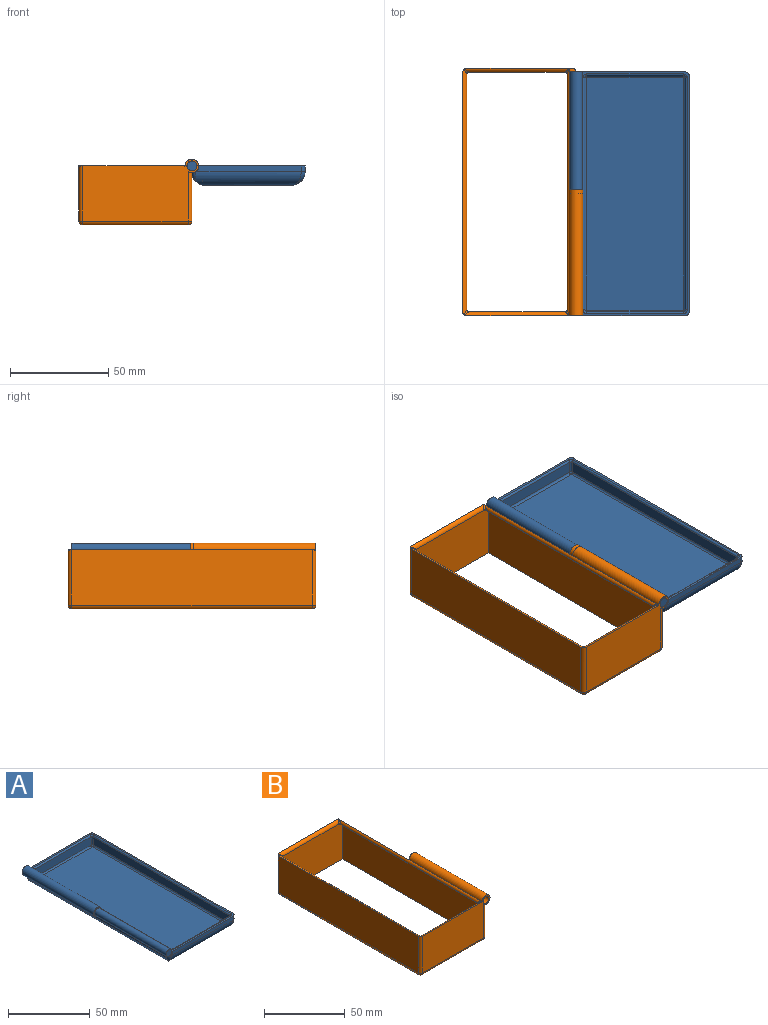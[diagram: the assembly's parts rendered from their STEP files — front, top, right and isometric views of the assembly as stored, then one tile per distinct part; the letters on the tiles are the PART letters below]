
ASSEMBLY  parts=2 mates=1
PART A: 48 faces, bbox 60.8x125.2x13.2 mm
  f0: cylinder r=7mm len=53.5mm, axis (1,0,0), area 556.8mm2, adj f5,f7,f40,f42,f45
  f1: plane 124x54.2mm, normal (0,0,1), area 244.1mm2, adj f2,f4,f5,f6,f8,f9,f19,f23
  f2: cylinder r=3.3mm len=62mm, axis (0,1,0), area 965mm2, adj f1,f3,f4,f5,f39,f45,f46
  f3: plane 119.94x1.63mm, normal (-1,0,0), area 182.9mm2, adj f2,f4,f6,f40,f45,f47
  f4: plane 6.8x6.8mm, normal (0,-1,0), area 15.6mm2, adj f1,f2,f3,f6,f10
  f5: plane 58.8x6.16mm, normal (0,1,0), area 183.8mm2, adj f0,f1,f2,f39,f41,f46
  f6: cylinder r=3.5mm len=62mm, axis (0,1,0), area 340mm2, adj f1,f3,f4,f9,f33,f38,f47
  f7: plane 110x43.81mm, normal (0,0,-1), area 4819.5mm2, adj f0,f37,f38,f40
  f8: plane 120x2.86mm, normal (1,0,0), area 343mm2, adj f1,f37,f41,f43
  f9: plane 53.48x2.86mm, normal (0,-1,0), area 149.9mm2, adj f1,f6,f38,f43
  f10: cylinder r=2.5mm len=62mm, axis (0,1,0), area 973.9mm2, adj f4,f11
  f11: plane 5x5mm, normal (0,-1,0), area 19.6mm2, adj f10
  f12: plane 118x6mm, normal (1,0,0), area 708mm2, adj f25,f30,f33,f36
  f13: plane 49x6mm, normal (0,1,0), area 294mm2, adj f22,f31,f32,f36
  f14: plane 118x6mm, normal (-1,0,0), area 708mm2, adj f17,f21,f22,f23
  f15: plane 49x6mm, normal (0,-1,0), area 294mm2, adj f17,f20,f24,f25
  f16: plane 118x49mm, normal (0,0,1), area 5782mm2, adj f20,f21,f30,f31
  f17: cylinder r=1mm len=6mm, axis (0,0,-1), area 9.4mm2, adj f14,f15,f18,f19
  f18: sphere r=1mm, area 1.6mm2, adj f17,f20,f21
  f19: torus R=2mm, axis (0,0,-1), area 3.4mm2, adj f1,f17,f23,f24
  f20: cylinder r=1mm len=49mm, axis (-1,0,0), area 77mm2, adj f15,f16,f18,f26
  f21: cylinder r=1mm len=118mm, axis (0,1,0), area 185.4mm2, adj f14,f16,f18,f27
  f22: cylinder r=1mm len=6mm, axis (0,0,1), area 9.4mm2, adj f13,f14,f27,f28
  f23: cylinder r=1mm len=118mm, axis (0,1,0), area 185.4mm2, adj f1,f14,f19,f28
  f24: cylinder r=1mm len=49mm, axis (-1,0,0), area 77mm2, adj f1,f15,f19,f29
  f25: cylinder r=1mm len=6mm, axis (0,0,1), area 9.4mm2, adj f12,f15,f26,f29
  f26: sphere r=1mm, area 1.6mm2, adj f20,f25,f30
  f27: sphere r=1mm, area 1.6mm2, adj f21,f22,f31
  f28: torus R=2mm, axis (0,0,-1), area 3.4mm2, adj f1,f22,f23,f32
  f29: torus R=2mm, axis (0,0,-1), area 3.4mm2, adj f1,f24,f25,f33
  f30: cylinder r=1mm len=118mm, axis (0,-1,0), area 185.4mm2, adj f12,f16,f26,f34
  f31: cylinder r=1mm len=49mm, axis (1,0,0), area 77mm2, adj f13,f16,f27,f34
  f32: cylinder r=1mm len=49mm, axis (1,0,0), area 77mm2, adj f1,f13,f28,f35
  f33: cylinder r=1mm len=118mm, axis (0,-1,0), area 185.4mm2, adj f1,f6,f12,f29,f35
  f34: sphere r=1mm, area 1.6mm2, adj f30,f31,f36
  f35: torus R=2mm, axis (0,0,-1), area 3.4mm2, adj f1,f32,f33,f36
  f36: cylinder r=1mm len=6mm, axis (0,0,-1), area 9.4mm2, adj f12,f13,f34,f35
  f37: cylinder r=7mm len=120mm, axis (0,-1,0), area 1279.5mm2, adj f7,f8,f42,f44
  f38: cylinder r=7mm len=53.5mm, axis (-1,0,0), area 556.8mm2, adj f6,f7,f9,f40,f44,f47
  f39: cylinder r=7mm len=3.3mm, axis (1,0,0), area 1mm2, adj f2,f5
  f40: cylinder r=7mm len=120.84mm, axis (0,1,0), area 1042.7mm2, adj f0,f3,f7,f38,f45,f47
  f41: cylinder r=2mm len=2.86mm, axis (0,0,1), area 9mm2, adj f1,f5,f8,f42
  f42: bspline ~8.17x7mm, area 23.6mm2, adj f0,f37,f41
  f43: cylinder r=2mm len=2.86mm, axis (0,0,-1), area 9mm2, adj f1,f8,f9,f44
  f44: bspline ~8.17x7mm, area 23.6mm2, adj f37,f38,f43
  f45: torus R=5mm, axis (-1,0,0), area 10.7mm2, adj f0,f2,f3,f40,f46
  f46: cylinder r=2mm len=0.35mm, axis (0,0,1), area 0mm2, adj f2,f5,f45
  f47: torus R=5mm, axis (-1,0,0), area 10.1mm2, adj f3,f6,f38,f40
PART B: 38 faces, bbox 61x126.5x33.5 mm
  f0: plane 120.02x0.27mm, normal (-1,0,0), area 32.2mm2, adj f13,f19,f20,f36
  f1: plane 122x24.5mm, normal (1,0,0), area 2989mm2, adj f2,f14,f22,f23,f24
  f2: cylinder r=3.5mm len=64mm, axis (0,1,0), area 1056.4mm2, adj f1,f5,f13,f15,f21,f22
  f3: plane 122x28mm, normal (-1,0,0), area 3416mm2, adj f10,f27,f30,f33
  f4: cylinder r=2.55mm len=64mm, axis (0,1,0), area 1025.4mm2, adj f5,f15
  f5: plane 59x31.5mm, normal (0,-1,0), area 1513mm2, adj f2,f4,f12,f21,f22,f27,f28
  f6: plane 53.5x28.03mm, normal (0,1,0), area 1495mm2, adj f11,f14,f17,f24,f29,f30
  f7: plane 122x28mm, normal (1,0,0), area 3416mm2, adj f8,f9,f10,f33,f34,f35
  f8: plane 53.5x28mm, normal (0,1,0), area 1498mm2, adj f7,f12,f28,f35,f36,f37
  f9: plane 53.5x28mm, normal (0,-1,0), area 1497.6mm2, adj f7,f11,f14,f29,f34,f36,f37
  f10: cylinder r=2mm len=124.58mm, axis (0,1,0), area 384.7mm2, adj f3,f7,f16,f18,f27,f30
  f11: cylinder r=2mm len=53.05mm, axis (1,0,0), area 159.4mm2, adj f6,f9,f16,f17,f19,f30
  f12: cylinder r=2mm len=53.05mm, axis (-1,0,0), area 159.4mm2, adj f5,f8,f18,f20,f21,f27
  f13: cylinder r=2mm len=124.23mm, axis (0,1,0), area 255.8mm2, adj f0,f2,f14,f17,f21
  f14: cylinder r=3.5mm len=62mm, axis (0,1,0), area 265.6mm2, adj f1,f6,f9,f13,f15,f17,f24,f36
  f15: plane 7x7mm, normal (0,1,0), area 17.6mm2, adj f2,f4,f14,f36,f37
  f16: bspline ~2.67x2.67mm, area 3.5mm2, adj f10,f11,f30,f34
  f17: bspline ~3.22x2.26mm, area 3.4mm2, adj f6,f11,f13,f14,f19
  f18: bspline ~2.67x2.67mm, area 3.5mm2, adj f10,f12,f27,f35
  f19: torus R=3mm, axis (-1,0,0), area 0.3mm2, adj f0,f11,f17,f36
  f20: torus R=3mm, axis (-1,0,0), area 0.3mm2, adj f0,f12,f21,f36
  f21: bspline ~3.22x2.26mm, area 3.4mm2, adj f2,f5,f12,f13,f20
  f22: cylinder r=2mm len=25.13mm, axis (0,0,-1), area 78mm2, adj f1,f2,f5,f25
  f23: cylinder r=2mm len=122mm, axis (0,-1,0), area 383.3mm2, adj f1,f25,f26,f37
  f24: cylinder r=2mm len=25.13mm, axis (0,0,1), area 78mm2, adj f1,f6,f14,f26
  f25: sphere r=2mm, area 6.3mm2, adj f22,f23,f28
  f26: sphere r=2mm, area 6.3mm2, adj f23,f24,f29
  f27: cylinder r=2mm len=28mm, axis (0,0,1), area 87.9mm2, adj f3,f5,f10,f12,f18,f31
  f28: cylinder r=2mm len=53.5mm, axis (-1,0,0), area 168.1mm2, adj f5,f8,f25,f31
  f29: cylinder r=2mm len=53.5mm, axis (1,0,0), area 168.1mm2, adj f6,f9,f26,f32
  f30: cylinder r=2mm len=28mm, axis (0,0,-1), area 87.9mm2, adj f3,f6,f10,f11,f16,f32
  f31: sphere r=2mm, area 6.3mm2, adj f27,f28,f33
  f32: sphere r=2mm, area 6.3mm2, adj f29,f30,f33
  f33: cylinder r=2mm len=122mm, axis (0,1,0), area 383.3mm2, adj f3,f7,f31,f32
  f34: plane 1.03x1.03mm, normal (0,0,-1), area 0.2mm2, adj f7,f9,f16
  f35: plane 1.03x1.03mm, normal (0,0,-1), area 0.2mm2, adj f7,f8,f18
  f36: plane 122x3.5mm, normal (0,0,-1), area 253.1mm2, adj f0,f8,f9,f14,f15,f19,f20,f37
  f37: plane 122x28mm, normal (-1,0,0), area 3363.7mm2, adj f8,f9,f14,f15,f23,f36
PLACE A t=(-29.52,-2,-44.22)mm
PLACE B t=(-3.75,0,1.21)mm
MATE revolute A.f2 <-> B.f2  axis (0,-1,0) through (-9.04,-126,-6.78)mm
